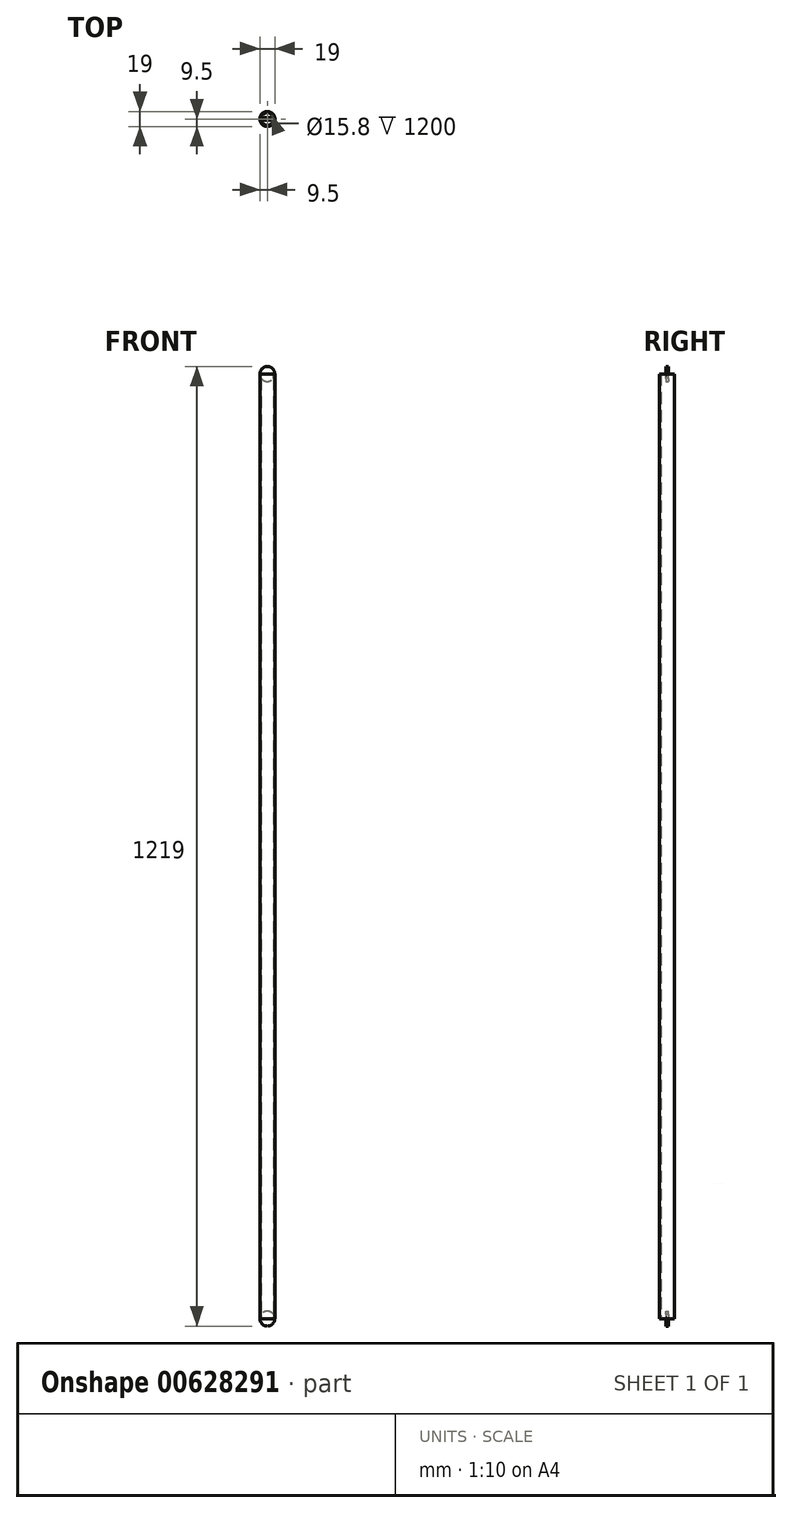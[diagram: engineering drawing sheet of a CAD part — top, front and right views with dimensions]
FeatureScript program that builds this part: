
annotation { "Feature Type Name" : "Feature", "Feature Type Description" : "" }
export const myFeature = defineFeature(function(context is Context, id is Id, definition is map)
    precondition{}
    {
        {
            var Q0;
            Q0=qCreatedBy(makeId("Top.planeOp"),FACE);
            var sketch = newSketch(context, id + "F0", { "sketchPlane" : qUnion([Q0])});
            skCircle(sketch, "E0", {"center": v(0, 0) * mm, "radius": 9.5 * mm});
            skCircle(sketch, "E1", {"center": v(0, 0) * mm, "radius": 7.9 * mm});
            skSolve(sketch);
        }
        {
            var Q0;
            Q0=makeQuery(id+"F0.imprint","IMPRINT",FACE,{"disambiguationData":[TD([[makeQuery(id+"F0.imprint","IMPRINT",EDGE,{"derivedFrom":sQuery(id+"F0.wireOp",EDGE,"E0")}),1.0]])]});
            extrude(context, id + "F1", {"entities" : qUnion([Q0]), "depth" : 600 * mm, "offsetDistance" : 25 * mm});
        }
        {
            var Q0;
            Q0=qCreatedBy(makeId("Front.planeOp"),FACE);
            var sketch = newSketch(context, id + "F2", { "sketchPlane" : qUnion([Q0])});
            skCircle(sketch, "E2", {"center": v(0, 0) * mm, "radius": 9.5 * mm});
            skSolve(sketch);
        }
        {
            var Q0;
            Q0=qSketchRegion(id+"F2",true);
            extrude(context, id + "F3", {"entities" : qUnion([Q0]), "operationType" : NewBodyOperationType.ADD, "depth" : 1.6 * mm, "offsetDistance" : 25 * mm});
        }
        {
            var Q0;
            Q0=makeQuery(id+"F3.opExtrude","CAP_FACE",FACE,{"disambiguationData":[OSD([sQuery(id+"F2.wireOp",EDGE,"E2")])],"isStart":true});
            extrude(context, id + "F4", {"entities" : qUnion([Q0]), "operationType" : NewBodyOperationType.ADD, "depth" : 1.6 * mm, "offsetDistance" : 25 * mm});
        }
        {
            var Q0;
            Q0=makeQuery(id+"F1.opExtrude","SWEPT_BODY",BODY,{"disambiguationData":[OSD([sQuery(id+"F0.wireOp",EDGE,"E0"),sQuery(id+"F0.wireOp",EDGE,"E1")])]});
            var Q1;
            Q1=makeQuery(id+"F1.opExtrude","CAP_FACE",FACE,{"disambiguationData":[OSD([sQuery(id+"F0.wireOp",EDGE,"E0"),sQuery(id+"F0.wireOp",EDGE,"E1")])],"isStart":false});
            mirror(context, id + "F5", {"operationType" : NewBodyOperationType.ADD, "entities" : qUnion([Q0]), "mirrorPlane" : qUnion([Q1])});
        }
    });
